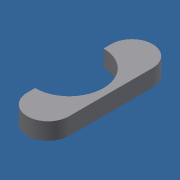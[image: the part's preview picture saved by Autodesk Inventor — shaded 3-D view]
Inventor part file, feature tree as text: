
AUTODESK INVENTOR PART (.ipt)
format: ipt  version: 2018 (Build 220112000, 112)  size: 92,160 bytes
history: native  units: mm
features: extrude x2, sketch x2, other x1
ambient origin geometry x8: Origin, YZ Plane, XZ Plane, XY Plane, X Axis, Y Axis, Z Axis, Center Point
bodies: Solid1 (feature_tree)
feature tree (5):
  other  "<userpath>\OneDrive\Objet3D\3DPrinter\Parameters.xlsx"
  extrude  "Extrusion1"  Depth=13.6mm
  extrude  "Extrusion2"  Depth=4.0mm
  sketch  "Sketch1"  dims[d0=16.0mm d1=13.6mm]
  sketch  "Sketch2"  dims[d3=4.0mm d4=0.0mm d5=16.2mm d6=0.0mm d7=0.0mm]
